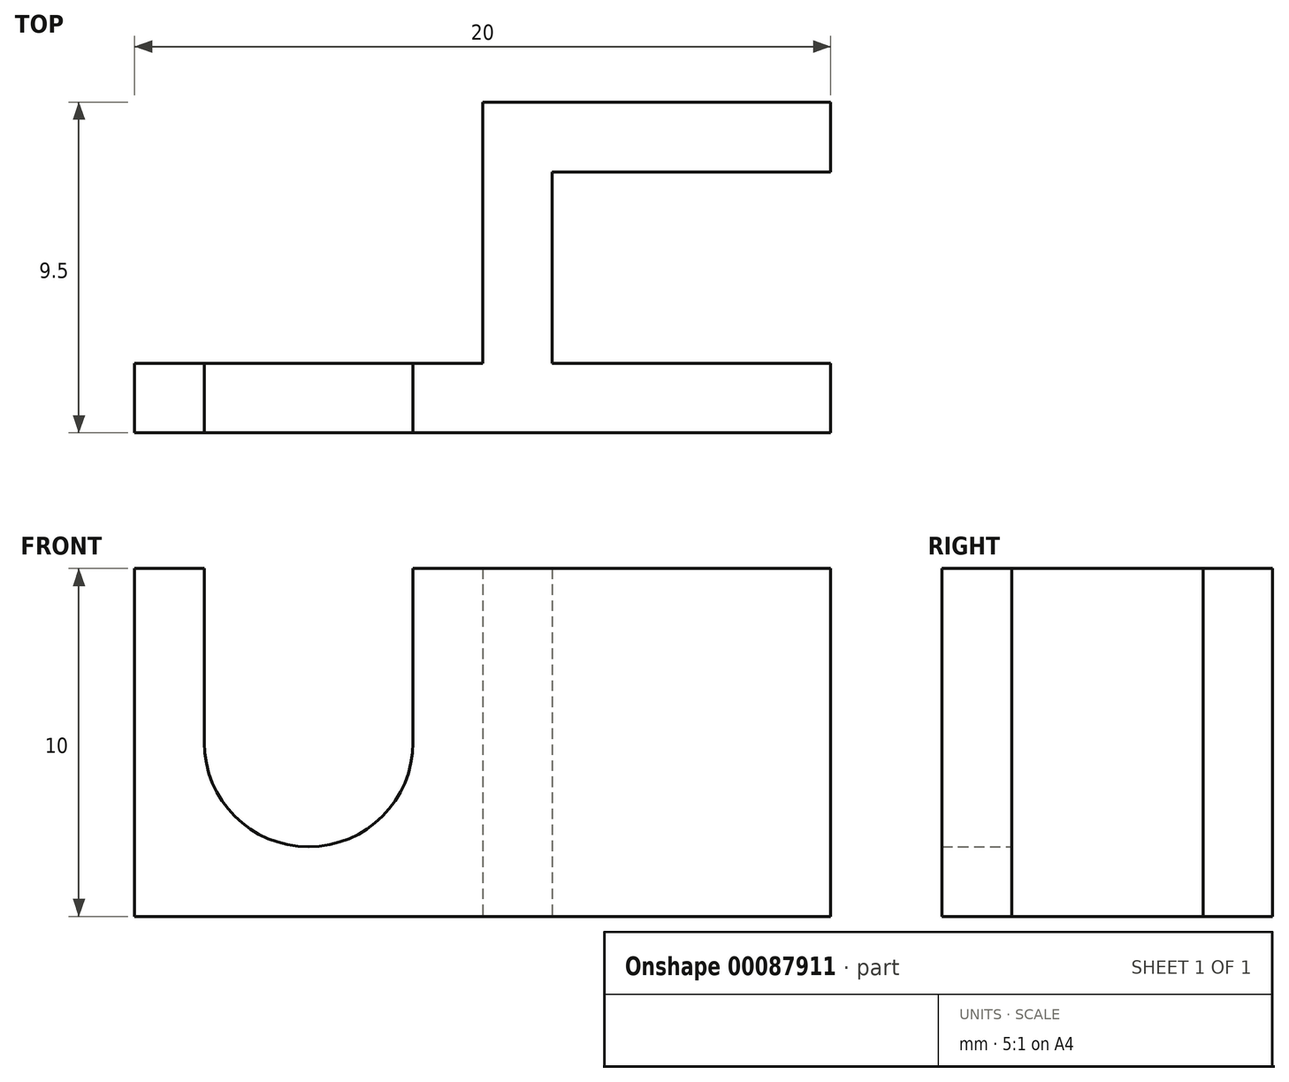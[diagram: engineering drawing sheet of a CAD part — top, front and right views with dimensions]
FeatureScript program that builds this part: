
annotation { "Feature Type Name" : "Feature", "Feature Type Description" : "" }
export const myFeature = defineFeature(function(context is Context, id is Id, definition is map)
    precondition{}
    {
        {
            var Q0;
            Q0=qCreatedBy(makeId("Top.planeOp"),FACE);
            var sketch = newSketch(context, id + "F0", { "sketchPlane" : qUnion([Q0])});
            skLineSegment(sketch, "E0.bottom", {"start": v(2, 0) * mm, "end": v(10, 0) * mm});
            skLineSegment(sketch, "E0.top", {"start": v(0, 2) * mm, "end": v(10, 2) * mm});
            skLineSegment(sketch, "E0.left", {"start": v(0, 0) * mm, "end": v(0, 2) * mm});
            skLineSegment(sketch, "E0.right", {"start": v(10, 0) * mm, "end": v(10, 2) * mm});
            skLineSegment(sketch, "E1.left", {"start": v(0, 0) * mm, "end": v(0, -5.5) * mm});
            skLineSegment(sketch, "E1.right", {"start": v(2, 0) * mm, "end": v(2, -5.5) * mm});
            skLineSegment(sketch, "E2.bottom", {"start": v(2, -5.5) * mm, "end": v(10, -5.5) * mm});
            skLineSegment(sketch, "E2.top", {"start": v(0, -7.5) * mm, "end": v(10, -7.5) * mm});
            skLineSegment(sketch, "E2.right", {"start": v(10, -5.5) * mm, "end": v(10, -7.5) * mm});
            skLineSegment(sketch, "E3.left", {"start": v(0, 2) * mm, "end": v(0, -5.5) * mm});
            skPoint(sketch, "E3.top.end.orphan", {"position": v(-10, -7.5) * mm});
            skLineSegment(sketch, "E4.bottom", {"start": v(0, -7.5) * mm, "end": v(-10, -7.5) * mm});
            skLineSegment(sketch, "E4.top", {"start": v(0, -5.5) * mm, "end": v(-10, -5.5) * mm});
            skLineSegment(sketch, "E4.right", {"start": v(-10, -7.5) * mm, "end": v(-10, -5.5) * mm});
            skSolve(sketch);
        }
        {
            var Q0;
            Q0=makeQuery(id+"F0.imprint","IMPRINT",FACE,{"disambiguationData":[TD([[makeQuery(id+"F0.imprint","IMPRINT",EDGE,{"derivedFrom":sQuery(id+"F0.wireOp",EDGE,"E0.bottom")}),1.0]])]});
            var Q1;
            Q1=makeQuery(id+"F0.imprint","IMPRINT",FACE,{"disambiguationData":[TD([[makeQuery(id+"F0.imprint","IMPRINT",EDGE,{"derivedFrom":sQuery(id+"F0.wireOp",EDGE,"E4.bottom")}),-1.0]])]});
            extrude(context, id + "F1", {"entities" : qUnion([Q0, Q1]), "depth" : 10 * mm});
        }
        {
            var Q0;
            Q0=makeQuery(id+"F1.opExtrude","SWEPT_FACE",FACE,{"disambiguationData":[OSD([sQuery(id+"F0.wireOp",EDGE,"E4.top")])]});
            var sketch = newSketch(context, id + "F2", { "sketchPlane" : qUnion([Q0])});
            skCircle(sketch, "E5", {"center": v(5, 5) * mm, "radius": 3 * mm});
            skPoint(sketch, "E6", {"position": v(5, 10) * mm});
            skLineSegment(sketch, "E7", {"start": v(2, 5) * mm, "end": v(2, 10) * mm});
            skLineSegment(sketch, "E8", {"start": v(8, 5) * mm, "end": v(8, 10) * mm});
            skSolve(sketch);
        }
        {
            var Q0;
            {var subQ0=sQuery(id+"F2.wireOp",EDGE,"E5");var subQ1=makeQuery(id+"F2.imprint","INTERSECT",VERTEX,{"derivedFrom":[subQ0,sQuery(id+"F2.wireOp",EDGE,"E7")]});Q0=makeQuery(id+"F2.imprint","IMPRINT",FACE,{"disambiguationData":[TD([[makeQuery(id+"F2.imprint","IMPRINT",EDGE,{"disambiguationData":[TD([[subQ1,1.0]])],"derivedFrom":subQ0}),1.0]])]});}
            var Q1;
            {var subQ0=sQuery(id+"F2.wireOp",EDGE,"E7");Q1=makeQuery(id+"F2.imprint","IMPRINT",FACE,{"disambiguationData":[TD([[makeQuery(id+"F2.imprint","IMPRINT",EDGE,{"derivedFrom":subQ0}),-1.0]])]});}
            extrude(context, id + "F3", {"entities" : qUnion([Q0, Q1]), "operationType" : NewBodyOperationType.REMOVE, "oppositeDirection" : true, "depth" : 25 * mm});
        }
    });
